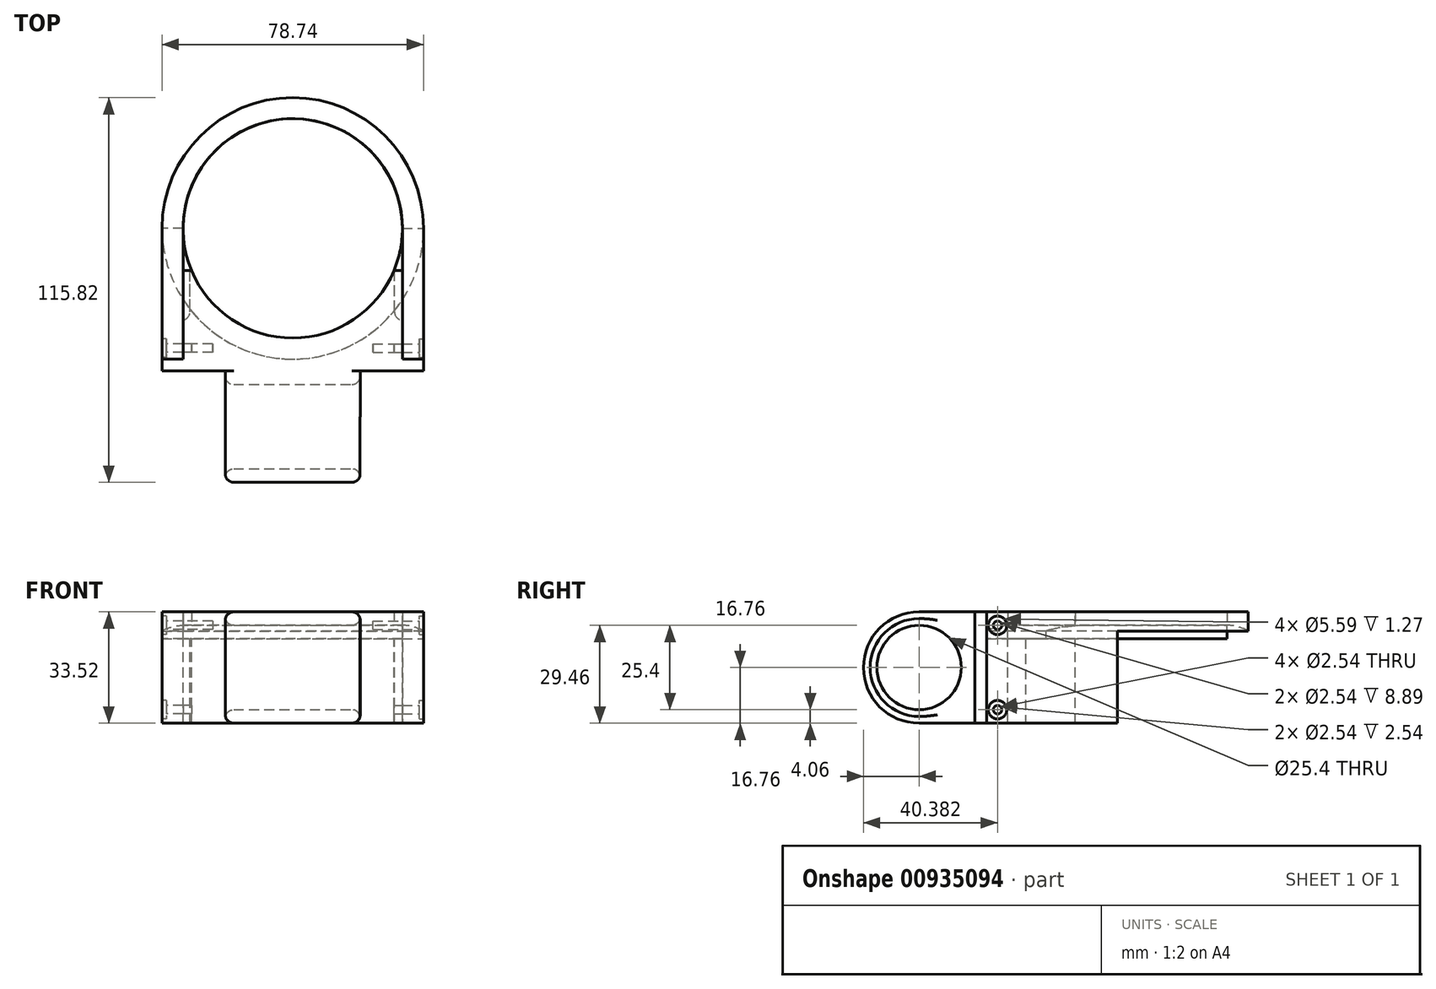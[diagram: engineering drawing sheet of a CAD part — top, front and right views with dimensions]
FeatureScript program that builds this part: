
annotation { "Feature Type Name" : "Feature", "Feature Type Description" : "" }
export const myFeature = defineFeature(function(context is Context, id is Id, definition is map)
    precondition{}
    {
        {
            var Q0;
            Q0=qCreatedBy(makeId("Top.planeOp"),FACE);
            var sketch = newSketch(context, id + "F0", { "sketchPlane" : qUnion([Q0])});
            skCircle(sketch, "E0", {"center": v(0, 0) * mm, "radius": 33.02 * mm});
            skCircle(sketch, "E1", {"center": v(0, 0) * mm, "radius": 39.37 * mm});
            skLineSegment(sketch, "E2", {"start": v(0, -39.37) * mm, "end": v(0, -59.7) * mm});
            skLineSegment(sketch, "E3", {"start": v(0, -59.7) * mm, "end": v(-19.05, -59.7) * mm});
            skLineSegment(sketch, "E4.bottom", {"start": v(-19.05, -59.7) * mm, "end": v(19.05, -59.7) * mm});
            skLineSegment(sketch, "E4.top", {"start": v(-19.05, -39.37) * mm, "end": v(19.05, -39.37) * mm});
            skLineSegment(sketch, "E4.left", {"start": v(-19.05, -59.7) * mm, "end": v(-19.05, -39.37) * mm});
            skLineSegment(sketch, "E4.right", {"start": v(19.05, -59.7) * mm, "end": v(19.05, -39.37) * mm});
            skPoint(sketch, "E4.middle", {"position": v(0, -49.53) * mm});
            skLineSegment(sketch, "E5.bottom", {"start": v(0, -59.7) * mm, "end": v(-39.37, -59.7) * mm});
            skLineSegment(sketch, "E5.top", {"start": v(0, 0) * mm, "end": v(-39.37, 0) * mm});
            skLineSegment(sketch, "E5.left", {"start": v(0, -59.7) * mm, "end": v(0, 0) * mm});
            skLineSegment(sketch, "E5.right", {"start": v(-39.37, -59.7) * mm, "end": v(-39.37, 0) * mm});
            skLineSegment(sketch, "E6.bottom", {"start": v(0, -59.7) * mm, "end": v(39.37, -59.7) * mm});
            skLineSegment(sketch, "E6.top", {"start": v(0, 0) * mm, "end": v(39.37, 0) * mm});
            skLineSegment(sketch, "E6.right", {"start": v(39.37, -59.7) * mm, "end": v(39.37, 0) * mm});
            skLineSegment(sketch, "E7", {"start": v(-33.02, 0) * mm, "end": v(-33.02, -59.7) * mm});
            skLineSegment(sketch, "E8", {"start": v(33.02, 0) * mm, "end": v(33.02, -59.7) * mm});
            skLineSegment(sketch, "E9", {"start": v(33.02, 0) * mm, "end": v(33.02, -12.7) * mm});
            skLineSegment(sketch, "E10", {"start": v(33.02, -12.7) * mm, "end": v(-33.02, -12.7) * mm});
            skLineSegment(sketch, "E11", {"start": v(-19.05, -39.37) * mm, "end": v(-39.37, -39.37) * mm});
            skLineSegment(sketch, "E12", {"start": v(-39.37, -39.37) * mm, "end": v(19.05, -39.37) * mm});
            skLineSegment(sketch, "E13", {"start": v(19.05, -39.37) * mm, "end": v(39.37, -39.37) * mm});
            skLineSegment(sketch, "E14", {"start": v(30.48, -12.7) * mm, "end": v(30.48, -24.92) * mm});
            skLineSegment(sketch, "E15", {"start": v(-30.48, -12.7) * mm, "end": v(-30.48, -24.92) * mm});
            skSolve(sketch);
        }
        {
            var Q0;
            {var subQ0=sQuery(id+"F0.wireOp",EDGE,"E5.top");var subQ1=sQuery(id+"F0.wireOp",EDGE,"E0");var subQ2=makeQuery(id+"F0.imprint","INTERSECT",VERTEX,{"derivedFrom":[subQ1,subQ0,sQuery(id+"F0.wireOp",EDGE,"E7")]});Q0=makeQuery(id+"F0.imprint","IMPRINT",FACE,{"disambiguationData":[TD([[makeQuery(id+"F0.imprint","IMPRINT",EDGE,{"disambiguationData":[TD([[subQ2,1.0]])],"derivedFrom":subQ1}),-1.0]])]});}
            var Q1;
            {var subQ1=sQuery(id+"F0.wireOp",EDGE,"E1");var subQ3=sQuery(id+"F0.wireOp",EDGE,"E8");var subQ4=makeQuery(id+"F0.imprint","INTERSECT",VERTEX,{"derivedFrom":[subQ1,subQ3]});Q1=makeQuery(id+"F0.imprint","IMPRINT",FACE,{"disambiguationData":[TD([[makeQuery(id+"F0.imprint","IMPRINT",EDGE,{"disambiguationData":[TD([[subQ4,1.0]])],"derivedFrom":subQ3}),1.0]])]});}
            var Q2;
            {var subQ3=sQuery(id+"F0.wireOp",EDGE,"E8");var subQ5=sQuery(id+"F0.wireOp",EDGE,"E13");var subQ7=makeQuery(id+"F0.imprint","INTERSECT",VERTEX,{"derivedFrom":[subQ3,subQ5]});Q2=makeQuery(id+"F0.imprint","IMPRINT",FACE,{"disambiguationData":[TD([[makeQuery(id+"F0.imprint","IMPRINT",EDGE,{"disambiguationData":[TD([[subQ7,1.0]])],"derivedFrom":subQ3}),1.0]])]});}
            var Q3;
            {var subQ1=sQuery(id+"F0.wireOp",EDGE,"E1");var subQ3=sQuery(id+"F0.wireOp",EDGE,"E7");var subQ4=makeQuery(id+"F0.imprint","INTERSECT",VERTEX,{"derivedFrom":[subQ1,subQ3]});Q3=makeQuery(id+"F0.imprint","IMPRINT",FACE,{"disambiguationData":[TD([[makeQuery(id+"F0.imprint","IMPRINT",EDGE,{"disambiguationData":[TD([[subQ4,1.0]])],"derivedFrom":subQ3}),-1.0]])]});}
            var Q4;
            {var subQ3=sQuery(id+"F0.wireOp",EDGE,"E7");var subQ5=sQuery(id+"F0.wireOp",EDGE,"E11");var subQ7=makeQuery(id+"F0.imprint","INTERSECT",VERTEX,{"derivedFrom":[subQ3,subQ5]});Q4=makeQuery(id+"F0.imprint","IMPRINT",FACE,{"disambiguationData":[TD([[makeQuery(id+"F0.imprint","IMPRINT",EDGE,{"disambiguationData":[TD([[subQ7,1.0]])],"derivedFrom":subQ3}),-1.0]])]});}
            extrude(context, id + "F1", {"entities" : qUnion([Q0, Q1, Q2, Q3, Q4]), "depth" : 4.06 * mm, "offsetDistance" : 25.4 * mm});
        }
        {
            var Q0;
            {var subQ3=sQuery(id+"F0.wireOp",EDGE,"E14");Q0=makeQuery(id+"F0.imprint","IMPRINT",FACE,{"disambiguationData":[TD([[makeQuery(id+"F0.imprint","IMPRINT",EDGE,{"derivedFrom":subQ3}),-1.0]])]});}
            var Q1;
            {var subQ1=sQuery(id+"F0.wireOp",EDGE,"E7");var subQ3=sQuery(id+"F0.wireOp",EDGE,"E1");var subQ4=makeQuery(id+"F0.imprint","INTERSECT",VERTEX,{"derivedFrom":[subQ3,subQ1]});Q1=makeQuery(id+"F0.imprint","IMPRINT",FACE,{"disambiguationData":[TD([[makeQuery(id+"F0.imprint","IMPRINT",EDGE,{"disambiguationData":[TD([[subQ4,-1.0]])],"derivedFrom":subQ3}),-1.0]])]});}
            var Q2;
            {var subQ1=sQuery(id+"F0.wireOp",EDGE,"E1");var subQ5=sQuery(id+"F0.wireOp",EDGE,"E8");var subQ7=makeQuery(id+"F0.imprint","INTERSECT",VERTEX,{"derivedFrom":[subQ1,subQ5]});Q2=makeQuery(id+"F0.imprint","IMPRINT",FACE,{"disambiguationData":[TD([[makeQuery(id+"F0.imprint","IMPRINT",EDGE,{"disambiguationData":[TD([[subQ7,1.0]])],"derivedFrom":subQ1}),-1.0]])]});}
            var Q3;
            {var subQ3=sQuery(id+"F0.wireOp",EDGE,"E15");Q3=makeQuery(id+"F0.imprint","IMPRINT",FACE,{"disambiguationData":[TD([[makeQuery(id+"F0.imprint","IMPRINT",EDGE,{"derivedFrom":subQ3}),1.0]])]});}
            var Q4;
            {var subQ3=sQuery(id+"F0.wireOp",EDGE,"E15");Q4=makeQuery(id+"F0.imprint","IMPRINT",FACE,{"disambiguationData":[TD([[makeQuery(id+"F0.imprint","IMPRINT",EDGE,{"derivedFrom":subQ3}),-1.0]])]});}
            var Q5;
            {var subQ3=sQuery(id+"F0.wireOp",EDGE,"E14");Q5=makeQuery(id+"F0.imprint","IMPRINT",FACE,{"disambiguationData":[TD([[makeQuery(id+"F0.imprint","IMPRINT",EDGE,{"derivedFrom":subQ3}),1.0]])]});}
            var Q6;
            {var subQ0=sQuery(id+"F0.wireOp",EDGE,"E5.right");var subQ1=sQuery(id+"F0.wireOp",EDGE,"E5.bottom");var subQ2=makeQuery(id+"F0.imprint","INTERSECT",VERTEX,{"derivedFrom":[subQ1,subQ0]});Q6=makeQuery(id+"F0.imprint","IMPRINT",FACE,{"disambiguationData":[TD([[makeQuery(id+"F0.imprint","IMPRINT",EDGE,{"disambiguationData":[TD([[subQ2,1.0]])],"derivedFrom":subQ1}),-1.0]])]});}
            var Q7;
            {var subQ0=sQuery(id+"F0.wireOp",EDGE,"E4.left");Q7=makeQuery(id+"F0.imprint","IMPRINT",FACE,{"disambiguationData":[TD([[makeQuery(id+"F0.imprint","IMPRINT",EDGE,{"derivedFrom":subQ0}),1.0]])]});}
            var Q8;
            {var subQ0=sQuery(id+"F0.wireOp",EDGE,"E2");Q8=makeQuery(id+"F0.imprint","IMPRINT",FACE,{"disambiguationData":[TD([[makeQuery(id+"F0.imprint","IMPRINT",EDGE,{"derivedFrom":subQ0}),-1.0]])]});}
            var Q9;
            {var subQ0=sQuery(id+"F0.wireOp",EDGE,"E2");Q9=makeQuery(id+"F0.imprint","IMPRINT",FACE,{"disambiguationData":[TD([[makeQuery(id+"F0.imprint","IMPRINT",EDGE,{"derivedFrom":subQ0}),1.0]])]});}
            var Q10;
            {var subQ0=sQuery(id+"F0.wireOp",EDGE,"E4.right");Q10=makeQuery(id+"F0.imprint","IMPRINT",FACE,{"disambiguationData":[TD([[makeQuery(id+"F0.imprint","IMPRINT",EDGE,{"derivedFrom":subQ0}),-1.0]])]});}
            var Q11;
            {var subQ0=sQuery(id+"F0.wireOp",EDGE,"E6.right");var subQ1=sQuery(id+"F0.wireOp",EDGE,"E6.bottom");var subQ2=makeQuery(id+"F0.imprint","INTERSECT",VERTEX,{"derivedFrom":[subQ1,subQ0]});Q11=makeQuery(id+"F0.imprint","IMPRINT",FACE,{"disambiguationData":[TD([[makeQuery(id+"F0.imprint","IMPRINT",EDGE,{"disambiguationData":[TD([[subQ2,1.0]])],"derivedFrom":subQ1}),1.0]])]});}
            extrude(context, id + "F2", {"entities" : qUnion([Q0, Q1, Q2, Q3, Q4, Q5, Q6, Q7, Q8, Q9, Q10, Q11]), "depth" : 4.06 * mm, "offsetDistance" : 25.4 * mm});
        }
        {
            var Q0;
            {var subQ0=sQuery(id+"F0.wireOp",EDGE,"E5.top");var subQ1=sQuery(id+"F0.wireOp",EDGE,"E0");var subQ2=makeQuery(id+"F0.imprint","INTERSECT",VERTEX,{"derivedFrom":[subQ1,subQ0,sQuery(id+"F0.wireOp",EDGE,"E7")]});Q0=makeQuery(id+"F0.imprint","IMPRINT",FACE,{"disambiguationData":[TD([[makeQuery(id+"F0.imprint","IMPRINT",EDGE,{"disambiguationData":[TD([[subQ2,1.0]])],"derivedFrom":subQ1}),1.0]])]});}
            var Q1;
            {var subQ0=sQuery(id+"F0.wireOp",EDGE,"E10");var subQ5=sQuery(id+"F0.wireOp",EDGE,"E5.left");var subQ7=makeQuery(id+"F0.imprint","INTERSECT",VERTEX,{"derivedFrom":[subQ5,subQ0]});Q1=makeQuery(id+"F0.imprint","IMPRINT",FACE,{"disambiguationData":[TD([[makeQuery(id+"F0.imprint","IMPRINT",EDGE,{"disambiguationData":[TD([[subQ7,-1.0]])],"derivedFrom":subQ5}),-1.0]])]});}
            var Q2;
            {var subQ0=sQuery(id+"F0.wireOp",EDGE,"E10");var subQ5=sQuery(id+"F0.wireOp",EDGE,"E5.left");var subQ7=makeQuery(id+"F0.imprint","INTERSECT",VERTEX,{"derivedFrom":[subQ5,subQ0]});Q2=makeQuery(id+"F0.imprint","IMPRINT",FACE,{"disambiguationData":[TD([[makeQuery(id+"F0.imprint","IMPRINT",EDGE,{"disambiguationData":[TD([[subQ7,-1.0]])],"derivedFrom":subQ5}),1.0]])]});}
            var Q3;
            {var subQ0=sQuery(id+"F0.wireOp",EDGE,"E5.left");var subQ1=sQuery(id+"F0.wireOp",EDGE,"E0");var subQ2=makeQuery(id+"F0.imprint","INTERSECT",VERTEX,{"derivedFrom":[subQ1,subQ0]});Q3=makeQuery(id+"F0.imprint","IMPRINT",FACE,{"disambiguationData":[TD([[makeQuery(id+"F0.imprint","IMPRINT",EDGE,{"disambiguationData":[TD([[subQ2,-1.0]])],"derivedFrom":subQ0}),1.0]])]});}
            var Q4;
            {var subQ0=sQuery(id+"F0.wireOp",EDGE,"E5.left");var subQ1=sQuery(id+"F0.wireOp",EDGE,"E0");var subQ2=makeQuery(id+"F0.imprint","INTERSECT",VERTEX,{"derivedFrom":[subQ1,subQ0]});Q4=makeQuery(id+"F0.imprint","IMPRINT",FACE,{"disambiguationData":[TD([[makeQuery(id+"F0.imprint","IMPRINT",EDGE,{"disambiguationData":[TD([[subQ2,-1.0]])],"derivedFrom":subQ0}),-1.0]])]});}
            extrude(context, id + "F3", {"entities" : qUnion([Q0, Q1, Q2, Q3, Q4]), "oppositeDirection" : true, "depth" : 4.06 * mm, "offsetDistance" : 25.4 * mm});
        }
        {
            var Q0;
            {var subQ0=sQuery(id+"F0.wireOp",EDGE,"E5.top");var subQ1=sQuery(id+"F0.wireOp",EDGE,"E0");var subQ2=makeQuery(id+"F0.imprint","INTERSECT",VERTEX,{"derivedFrom":[subQ1,subQ0,sQuery(id+"F0.wireOp",EDGE,"E7")]});Q0=makeQuery(id+"F0.imprint","IMPRINT",FACE,{"disambiguationData":[TD([[makeQuery(id+"F0.imprint","IMPRINT",EDGE,{"disambiguationData":[TD([[subQ2,1.0]])],"derivedFrom":subQ1}),-1.0]])]});}
            extrude(context, id + "F4", {"entities" : qUnion([Q0]), "oppositeDirection" : true, "depth" : 4.06 * mm, "offsetDistance" : 25.4 * mm});
        }
        {
            var Q0;
            {var subQ0=sQuery(id+"F0.wireOp",EDGE,"E5.right");var subQ1=sQuery(id+"F0.wireOp",EDGE,"E5.bottom");var subQ2=makeQuery(id+"F0.imprint","INTERSECT",VERTEX,{"derivedFrom":[subQ1,subQ0]});Q0=makeQuery(id+"F0.imprint","IMPRINT",FACE,{"disambiguationData":[TD([[makeQuery(id+"F0.imprint","IMPRINT",EDGE,{"disambiguationData":[TD([[subQ2,1.0]])],"derivedFrom":subQ1}),-1.0]])]});}
            var Q1;
            {var subQ0=sQuery(id+"F0.wireOp",EDGE,"E4.left");Q1=makeQuery(id+"F0.imprint","IMPRINT",FACE,{"disambiguationData":[TD([[makeQuery(id+"F0.imprint","IMPRINT",EDGE,{"derivedFrom":subQ0}),1.0]])]});}
            var Q2;
            {var subQ1=sQuery(id+"F0.wireOp",EDGE,"E7");var subQ3=sQuery(id+"F0.wireOp",EDGE,"E1");var subQ4=makeQuery(id+"F0.imprint","INTERSECT",VERTEX,{"derivedFrom":[subQ3,subQ1]});Q2=makeQuery(id+"F0.imprint","IMPRINT",FACE,{"disambiguationData":[TD([[makeQuery(id+"F0.imprint","IMPRINT",EDGE,{"disambiguationData":[TD([[subQ4,-1.0]])],"derivedFrom":subQ3}),-1.0]])]});}
            var Q3;
            {var subQ0=sQuery(id+"F0.wireOp",EDGE,"E2");Q3=makeQuery(id+"F0.imprint","IMPRINT",FACE,{"disambiguationData":[TD([[makeQuery(id+"F0.imprint","IMPRINT",EDGE,{"derivedFrom":subQ0}),-1.0]])]});}
            var Q4;
            {var subQ0=sQuery(id+"F0.wireOp",EDGE,"E2");Q4=makeQuery(id+"F0.imprint","IMPRINT",FACE,{"disambiguationData":[TD([[makeQuery(id+"F0.imprint","IMPRINT",EDGE,{"derivedFrom":subQ0}),1.0]])]});}
            var Q5;
            {var subQ0=sQuery(id+"F0.wireOp",EDGE,"E4.right");Q5=makeQuery(id+"F0.imprint","IMPRINT",FACE,{"disambiguationData":[TD([[makeQuery(id+"F0.imprint","IMPRINT",EDGE,{"derivedFrom":subQ0}),-1.0]])]});}
            var Q6;
            {var subQ0=sQuery(id+"F0.wireOp",EDGE,"E6.right");var subQ1=sQuery(id+"F0.wireOp",EDGE,"E6.bottom");var subQ2=makeQuery(id+"F0.imprint","INTERSECT",VERTEX,{"derivedFrom":[subQ1,subQ0]});Q6=makeQuery(id+"F0.imprint","IMPRINT",FACE,{"disambiguationData":[TD([[makeQuery(id+"F0.imprint","IMPRINT",EDGE,{"disambiguationData":[TD([[subQ2,1.0]])],"derivedFrom":subQ1}),1.0]])]});}
            var Q7;
            {var subQ1=sQuery(id+"F0.wireOp",EDGE,"E1");var subQ5=sQuery(id+"F0.wireOp",EDGE,"E8");var subQ7=makeQuery(id+"F0.imprint","INTERSECT",VERTEX,{"derivedFrom":[subQ1,subQ5]});Q7=makeQuery(id+"F0.imprint","IMPRINT",FACE,{"disambiguationData":[TD([[makeQuery(id+"F0.imprint","IMPRINT",EDGE,{"disambiguationData":[TD([[subQ7,1.0]])],"derivedFrom":subQ1}),-1.0]])]});}
            var Q8;
            {var subQ3=sQuery(id+"F0.wireOp",EDGE,"E14");Q8=makeQuery(id+"F0.imprint","IMPRINT",FACE,{"disambiguationData":[TD([[makeQuery(id+"F0.imprint","IMPRINT",EDGE,{"derivedFrom":subQ3}),-1.0]])]});}
            var Q9;
            {var subQ3=sQuery(id+"F0.wireOp",EDGE,"E15");Q9=makeQuery(id+"F0.imprint","IMPRINT",FACE,{"disambiguationData":[TD([[makeQuery(id+"F0.imprint","IMPRINT",EDGE,{"derivedFrom":subQ3}),-1.0]])]});}
            var Q10;
            {var subQ3=sQuery(id+"F0.wireOp",EDGE,"E15");Q10=makeQuery(id+"F0.imprint","IMPRINT",FACE,{"disambiguationData":[TD([[makeQuery(id+"F0.imprint","IMPRINT",EDGE,{"derivedFrom":subQ3}),1.0]])]});}
            var Q11;
            {var subQ3=sQuery(id+"F0.wireOp",EDGE,"E14");Q11=makeQuery(id+"F0.imprint","IMPRINT",FACE,{"disambiguationData":[TD([[makeQuery(id+"F0.imprint","IMPRINT",EDGE,{"derivedFrom":subQ3}),1.0]])]});}
            extrude(context, id + "F5", {"entities" : qUnion([Q0, Q1, Q2, Q3, Q4, Q5, Q6, Q7, Q8, Q9, Q10, Q11]), "oppositeDirection" : true, "depth" : 4.06 * mm, "offsetDistance" : 25.4 * mm});
        }
        {
            var Q0;
            {var subQ3=sQuery(id+"F0.wireOp",EDGE,"E7");var subQ5=sQuery(id+"F0.wireOp",EDGE,"E11");var subQ7=makeQuery(id+"F0.imprint","INTERSECT",VERTEX,{"derivedFrom":[subQ3,subQ5]});Q0=makeQuery(id+"F0.imprint","IMPRINT",FACE,{"disambiguationData":[TD([[makeQuery(id+"F0.imprint","IMPRINT",EDGE,{"disambiguationData":[TD([[subQ7,1.0]])],"derivedFrom":subQ3}),-1.0]])]});}
            var Q1;
            {var subQ1=sQuery(id+"F0.wireOp",EDGE,"E1");var subQ3=sQuery(id+"F0.wireOp",EDGE,"E7");var subQ4=makeQuery(id+"F0.imprint","INTERSECT",VERTEX,{"derivedFrom":[subQ1,subQ3]});Q1=makeQuery(id+"F0.imprint","IMPRINT",FACE,{"disambiguationData":[TD([[makeQuery(id+"F0.imprint","IMPRINT",EDGE,{"disambiguationData":[TD([[subQ4,1.0]])],"derivedFrom":subQ3}),-1.0]])]});}
            var Q2;
            {var subQ1=sQuery(id+"F0.wireOp",EDGE,"E1");var subQ3=sQuery(id+"F0.wireOp",EDGE,"E8");var subQ4=makeQuery(id+"F0.imprint","INTERSECT",VERTEX,{"derivedFrom":[subQ1,subQ3]});Q2=makeQuery(id+"F0.imprint","IMPRINT",FACE,{"disambiguationData":[TD([[makeQuery(id+"F0.imprint","IMPRINT",EDGE,{"disambiguationData":[TD([[subQ4,1.0]])],"derivedFrom":subQ3}),1.0]])]});}
            var Q3;
            {var subQ3=sQuery(id+"F0.wireOp",EDGE,"E8");var subQ5=sQuery(id+"F0.wireOp",EDGE,"E13");var subQ7=makeQuery(id+"F0.imprint","INTERSECT",VERTEX,{"derivedFrom":[subQ3,subQ5]});Q3=makeQuery(id+"F0.imprint","IMPRINT",FACE,{"disambiguationData":[TD([[makeQuery(id+"F0.imprint","IMPRINT",EDGE,{"disambiguationData":[TD([[subQ7,1.0]])],"derivedFrom":subQ3}),1.0]])]});}
            extrude(context, id + "F6", {"entities" : qUnion([Q0, Q1, Q2, Q3]), "oppositeDirection" : true, "depth" : 4.06 * mm, "offsetDistance" : 25.4 * mm});
        }
        {
            var Q0;
            Q0=makeQuery(id+"F6.opExtrude","SWEPT_FACE",FACE,{"disambiguationData":[OSD([sQuery(id+"F0.wireOp",EDGE,"E5.top")])]});
            var sketch = newSketch(context, id + "F7", { "sketchPlane" : qUnion([Q0])});
            skLineSegment(sketch, "E16", {"start": v(33.02, 0) * mm, "end": v(33.02, -12.7) * mm});
            skArc(sketch, "E17", {"start": v(33.02, 0) * mm, "mid": v(42, -3.72) * mm, "end": v(45.72, -12.7) * mm});
            skLineSegment(sketch, "E18", {"start": v(33.02, -12.7) * mm, "end": v(45.72, -12.7) * mm});
            skLineSegment(sketch, "E19", {"start": v(33.02, -12.7) * mm, "end": v(33.02, -38.1) * mm});
            skLineSegment(sketch, "E20.bottom", {"start": v(45.72, -12.7) * mm, "end": v(33.02, -12.7) * mm});
            skLineSegment(sketch, "E20.top", {"start": v(45.72, -38.1) * mm, "end": v(33.02, -38.1) * mm});
            skLineSegment(sketch, "E20.left", {"start": v(45.72, -12.7) * mm, "end": v(45.72, -38.1) * mm});
            skSolve(sketch);
        }
        {
            var Q0;
            Q0=makeQuery(id+"F5.opExtrude","CAP_FACE",FACE,{"disambiguationData":[OSD([sQuery(id+"F0.wireOp",EDGE,"E0"),sQuery(id+"F0.wireOp",EDGE,"E3"),sQuery(id+"F0.wireOp",EDGE,"E4.bottom"),sQuery(id+"F0.wireOp",EDGE,"E5.bottom"),sQuery(id+"F0.wireOp",EDGE,"E5.right"),sQuery(id+"F0.wireOp",EDGE,"E6.bottom"),sQuery(id+"F0.wireOp",EDGE,"E6.right"),sQuery(id+"F0.wireOp",EDGE,"E7"),sQuery(id+"F0.wireOp",EDGE,"E8"),sQuery(id+"F0.wireOp",EDGE,"E10"),sQuery(id+"F0.wireOp",EDGE,"E11"),sQuery(id+"F0.wireOp",EDGE,"E13")])],"isStart":false});
            var Q1;
            Q1=makeQuery(id+"F6.opExtrude","CAP_FACE",FACE,{"disambiguationData":[OSD([sQuery(id+"F0.wireOp",EDGE,"E5.top"),sQuery(id+"F0.wireOp",EDGE,"E5.right"),sQuery(id+"F0.wireOp",EDGE,"E7"),sQuery(id+"F0.wireOp",EDGE,"E11")])],"isStart":false});
            var Q2;
            Q2=makeQuery(id+"F6.opExtrude","CAP_FACE",FACE,{"disambiguationData":[OSD([sQuery(id+"F0.wireOp",EDGE,"E6.top"),sQuery(id+"F0.wireOp",EDGE,"E6.right"),sQuery(id+"F0.wireOp",EDGE,"E8"),sQuery(id+"F0.wireOp",EDGE,"E13")])],"isStart":false});
            extrude(context, id + "F8", {"entities" : qUnion([Q0, Q1, Q2]), "depth" : 25.4 * mm, "offsetDistance" : 25.4 * mm});
        }
        {
            var Q0;
            {var subQ2=sQuery(id+"F7.wireOp",EDGE,"E20.bottom");Q0=makeQuery(id+"F7.imprint","IMPRINT",FACE,{"disambiguationData":[TD([[makeQuery(id+"F7.imprint","IMPRINT",EDGE,{"derivedFrom":subQ2}),-1.0]])]});}
            var Q1;
            Q1=makeQuery(id+"F7.imprint","IMPRINT",FACE,{"disambiguationData":[TD([[makeQuery(id+"F7.imprint","IMPRINT",EDGE,{"derivedFrom":sQuery(id+"F7.wireOp",EDGE,"E20.bottom")}),1.0]])]});
            var Q2;
            {var subQ2=sQuery(id+"F0.wireOp",EDGE,"E5.top");var subQ4=makeQuery(id+"F6.opExtrude","CAP_EDGE",EDGE,{"disambiguationData":[OSD([subQ2])],"isStart":false});Q2=makeQuery(id+"F7.imprint","IMPRINT",FACE,{"disambiguationData":[TD([[makeQuery(id+"F7.imprint","IMPRINT",EDGE,{"derivedFrom":subQ4}),1.0]])]});}
            var Q3;
            Q3=makeQuery(id+"F1.opExtrude","CAP_EDGE",EDGE,{"disambiguationData":[OSD([sQuery(id+"F0.wireOp",EDGE,"E0")])],"isStart":true});
            revolve(context, id + "F9", {"operationType" : NewBodyOperationType.REMOVE, "surfaceOperationType" : NewSurfaceOperationType.NEW, "entities" : qUnion([Q0, Q1, Q2]), "axis" : qUnion([Q3]), "revolveType" : RevolveType.FULL, "oppositeDirection" : true});
        }
        {
            var Q0;
            Q0=makeQuery(id+"F8.opExtrude","CAP_FACE",FACE,{"disambiguationData":[OSD([sQuery(id+"F0.wireOp",EDGE,"E5.top"),sQuery(id+"F0.wireOp",EDGE,"E5.right"),sQuery(id+"F0.wireOp",EDGE,"E7"),sQuery(id+"F0.wireOp",EDGE,"E11")])],"isStart":false});
            var sketch = newSketch(context, id + "F10", { "sketchPlane" : qUnion([Q0])});
            skLineSegment(sketch, "E21", {"start": v(-36.44, 27.62) * mm, "end": v(-39.37, 27.62) * mm});
            skLineSegment(sketch, "E22.bottom", {"start": v(-39.37, 27.62) * mm, "end": v(-30.94, 27.62) * mm});
            skLineSegment(sketch, "E22.top", {"start": v(-39.37, 8.01) * mm, "end": v(-30.94, 8.01) * mm});
            skLineSegment(sketch, "E22.left", {"start": v(-39.37, 27.62) * mm, "end": v(-39.37, 8.01) * mm});
            skLineSegment(sketch, "E22.right", {"start": v(-30.94, 27.62) * mm, "end": v(-30.94, 8.01) * mm});
            skSolve(sketch);
        }
        {
            var Q0;
            Q0=makeQuery(id+"F8.opExtrude","CAP_FACE",FACE,{"disambiguationData":[OSD([sQuery(id+"F0.wireOp",EDGE,"E6.top"),sQuery(id+"F0.wireOp",EDGE,"E6.right"),sQuery(id+"F0.wireOp",EDGE,"E8"),sQuery(id+"F0.wireOp",EDGE,"E13")])],"isStart":false});
            var sketch = newSketch(context, id + "F11", { "sketchPlane" : qUnion([Q0])});
            skLineSegment(sketch, "E23", {"start": v(36.44, 27.62) * mm, "end": v(39.37, 27.62) * mm});
            skLineSegment(sketch, "E24.bottom", {"start": v(39.37, 27.62) * mm, "end": v(30.62, 27.62) * mm});
            skLineSegment(sketch, "E24.top", {"start": v(39.37, 1.89) * mm, "end": v(30.62, 1.89) * mm});
            skLineSegment(sketch, "E24.left", {"start": v(39.37, 27.62) * mm, "end": v(39.37, 1.89) * mm});
            skLineSegment(sketch, "E24.right", {"start": v(30.62, 27.62) * mm, "end": v(30.62, 1.89) * mm});
            skSolve(sketch);
        }
        {
            var Q0;
            {var subQ0=sQuery(id+"F11.wireOp",EDGE,"E24.left");var subQ1=sQuery(id+"F11.wireOp",EDGE,"E24.bottom");var subQ2=sQuery(id+"F0.wireOp",EDGE,"E6.right");var subQ3=makeQuery(id+"F11.imprint","INTERSECT",VERTEX,{"derivedFrom":[makeQuery(id+"F8.opExtrude","CAP_EDGE",EDGE,{"disambiguationData":[OSD([subQ2]),TDD([makeQuery(id+"F6.opExtrude","CAP_EDGE",EDGE,{"disambiguationData":[OSD([subQ2])],"isStart":false})])],"isStart":false}),subQ1,subQ0]});Q0=makeQuery(id+"F11.imprint","IMPRINT",FACE,{"disambiguationData":[TD([[makeQuery(id+"F11.imprint","IMPRINT",EDGE,{"disambiguationData":[TD([[subQ3,-1.0]])],"derivedFrom":subQ1}),1.0]])]});}
            var Q1;
            {var subQ4=sQuery(id+"F11.wireOp",EDGE,"E24.top");Q1=makeQuery(id+"F11.imprint","IMPRINT",FACE,{"disambiguationData":[TD([[makeQuery(id+"F11.imprint","IMPRINT",EDGE,{"derivedFrom":subQ4}),-1.0]])]});}
            var Q2;
            {var subQ4=sQuery(id+"F10.wireOp",EDGE,"E22.top");Q2=makeQuery(id+"F10.imprint","IMPRINT",FACE,{"disambiguationData":[TD([[makeQuery(id+"F10.imprint","IMPRINT",EDGE,{"derivedFrom":subQ4}),1.0]])]});}
            var Q3;
            {var subQ0=sQuery(id+"F10.wireOp",EDGE,"E22.left");var subQ1=sQuery(id+"F10.wireOp",EDGE,"E22.bottom");var subQ2=sQuery(id+"F0.wireOp",EDGE,"E5.right");var subQ3=makeQuery(id+"F10.imprint","INTERSECT",VERTEX,{"derivedFrom":[makeQuery(id+"F8.opExtrude","CAP_EDGE",EDGE,{"disambiguationData":[OSD([subQ2]),TDD([makeQuery(id+"F6.opExtrude","CAP_EDGE",EDGE,{"disambiguationData":[OSD([subQ2])],"isStart":false})])],"isStart":false}),subQ1,subQ0]});Q3=makeQuery(id+"F10.imprint","IMPRINT",FACE,{"disambiguationData":[TD([[makeQuery(id+"F10.imprint","IMPRINT",EDGE,{"disambiguationData":[TD([[subQ3,-1.0]])],"derivedFrom":subQ1}),-1.0]])]});}
            extrude(context, id + "F12", {"entities" : qUnion([Q0, Q1, Q2, Q3]), "operationType" : NewBodyOperationType.REMOVE, "oppositeDirection" : true, "depth" : 25.4 * mm, "offsetDistance" : 25.4 * mm});
        }
        {
            var Q0;
            Q0=makeQuery(id+"F8.opExtrude","SWEPT_BODY",BODY,{"disambiguationData":[OSD([sQuery(id+"F0.wireOp",EDGE,"E5.top"),sQuery(id+"F0.wireOp",EDGE,"E5.right"),sQuery(id+"F0.wireOp",EDGE,"E7"),sQuery(id+"F0.wireOp",EDGE,"E11")])]});
            var Q1;
            Q1=makeQuery(id+"F6.opExtrude","SWEPT_BODY",BODY,{"disambiguationData":[OSD([sQuery(id+"F0.wireOp",EDGE,"E5.top"),sQuery(id+"F0.wireOp",EDGE,"E5.right"),sQuery(id+"F0.wireOp",EDGE,"E7"),sQuery(id+"F0.wireOp",EDGE,"E11")])]});
            var Q2;
            Q2=makeQuery(id+"F1.opExtrude","SWEPT_BODY",BODY,{"disambiguationData":[OSD([sQuery(id+"F0.wireOp",EDGE,"E0"),sQuery(id+"F0.wireOp",EDGE,"E1"),sQuery(id+"F0.wireOp",EDGE,"E5.right"),sQuery(id+"F0.wireOp",EDGE,"E6.right"),sQuery(id+"F0.wireOp",EDGE,"E7"),sQuery(id+"F0.wireOp",EDGE,"E8"),sQuery(id+"F0.wireOp",EDGE,"E11"),sQuery(id+"F0.wireOp",EDGE,"E13")])]});
            var Q3;
            Q3=makeQuery(id+"F4.opExtrude","SWEPT_BODY",BODY,{"disambiguationData":[OSD([sQuery(id+"F0.wireOp",EDGE,"E0"),sQuery(id+"F0.wireOp",EDGE,"E1"),sQuery(id+"F0.wireOp",EDGE,"E5.top"),sQuery(id+"F0.wireOp",EDGE,"E6.top")])]});
            var Q4;
            Q4=makeQuery(id+"F6.opExtrude","SWEPT_BODY",BODY,{"disambiguationData":[OSD([sQuery(id+"F0.wireOp",EDGE,"E6.top"),sQuery(id+"F0.wireOp",EDGE,"E6.right"),sQuery(id+"F0.wireOp",EDGE,"E8"),sQuery(id+"F0.wireOp",EDGE,"E13")])]});
            var Q5;
            Q5=makeQuery(id+"F8.opExtrude","SWEPT_BODY",BODY,{"disambiguationData":[OSD([sQuery(id+"F0.wireOp",EDGE,"E6.top"),sQuery(id+"F0.wireOp",EDGE,"E6.right"),sQuery(id+"F0.wireOp",EDGE,"E8"),sQuery(id+"F0.wireOp",EDGE,"E13")])]});
            booleanBodies(context, id + "F13", {"operationType" : BooleanOperationType.UNION, "tools" : qUnion([Q0, Q1, Q2, Q3, Q4, Q5])});
        }
        {
            var Q0;
            Q0=makeQuery(id+"F8.opExtrude","SWEPT_BODY",BODY,{"disambiguationData":[OSD([sQuery(id+"F0.wireOp",EDGE,"E0"),sQuery(id+"F0.wireOp",EDGE,"E3"),sQuery(id+"F0.wireOp",EDGE,"E4.bottom"),sQuery(id+"F0.wireOp",EDGE,"E5.bottom"),sQuery(id+"F0.wireOp",EDGE,"E5.right"),sQuery(id+"F0.wireOp",EDGE,"E6.bottom"),sQuery(id+"F0.wireOp",EDGE,"E6.right"),sQuery(id+"F0.wireOp",EDGE,"E7"),sQuery(id+"F0.wireOp",EDGE,"E8"),sQuery(id+"F0.wireOp",EDGE,"E10"),sQuery(id+"F0.wireOp",EDGE,"E11"),sQuery(id+"F0.wireOp",EDGE,"E13")])]});
            var Q1;
            Q1=makeQuery(id+"F5.opExtrude","SWEPT_BODY",BODY,{"disambiguationData":[OSD([sQuery(id+"F0.wireOp",EDGE,"E0"),sQuery(id+"F0.wireOp",EDGE,"E3"),sQuery(id+"F0.wireOp",EDGE,"E4.bottom"),sQuery(id+"F0.wireOp",EDGE,"E5.bottom"),sQuery(id+"F0.wireOp",EDGE,"E5.right"),sQuery(id+"F0.wireOp",EDGE,"E6.bottom"),sQuery(id+"F0.wireOp",EDGE,"E6.right"),sQuery(id+"F0.wireOp",EDGE,"E7"),sQuery(id+"F0.wireOp",EDGE,"E8"),sQuery(id+"F0.wireOp",EDGE,"E10"),sQuery(id+"F0.wireOp",EDGE,"E11"),sQuery(id+"F0.wireOp",EDGE,"E13")])]});
            var Q2;
            Q2=makeQuery(id+"F2.opExtrude","SWEPT_BODY",BODY,{"disambiguationData":[OSD([sQuery(id+"F0.wireOp",EDGE,"E0"),sQuery(id+"F0.wireOp",EDGE,"E3"),sQuery(id+"F0.wireOp",EDGE,"E4.bottom"),sQuery(id+"F0.wireOp",EDGE,"E5.bottom"),sQuery(id+"F0.wireOp",EDGE,"E5.right"),sQuery(id+"F0.wireOp",EDGE,"E6.bottom"),sQuery(id+"F0.wireOp",EDGE,"E6.right"),sQuery(id+"F0.wireOp",EDGE,"E7"),sQuery(id+"F0.wireOp",EDGE,"E8"),sQuery(id+"F0.wireOp",EDGE,"E10"),sQuery(id+"F0.wireOp",EDGE,"E11"),sQuery(id+"F0.wireOp",EDGE,"E13")])]});
            booleanBodies(context, id + "F14", {"operationType" : BooleanOperationType.UNION, "tools" : qUnion([Q0, Q1, Q2])});
        }
        {
            var Q0;
            {var subQ0=sQuery(id+"F0.wireOp",EDGE,"E5.right");Q0=makeQuery(id+"F13.opBoolean","MERGE",FACE,{"derivedFrom":[makeQuery(id+"F1.opExtrude","SWEPT_FACE",FACE,{"disambiguationData":[OSD([subQ0])]}),makeQuery(id+"F6.opExtrude","SWEPT_FACE",FACE,{"disambiguationData":[OSD([subQ0])]}),makeQuery(id+"F8.opExtrude","SWEPT_FACE",FACE,{"disambiguationData":[OSD([subQ0]),TDD([makeQuery(id+"F6.opExtrude","CAP_EDGE",EDGE,{"disambiguationData":[OSD([subQ0])],"isStart":false})])]})]});}
            var sketch = newSketch(context, id + "F15", { "sketchPlane" : qUnion([Q0])});
            skLineSegment(sketch, "E25", {"start": v(39.37, 0) * mm, "end": v(36.07, 0) * mm});
            skCircle(sketch, "E26", {"center": v(36.07, 0) * mm, "radius": 2.8 * mm});
            skLineSegment(sketch, "E27", {"start": v(39.37, 0) * mm, "end": v(39.37, -25.4) * mm});
            skLineSegment(sketch, "E28", {"start": v(39.37, -25.4) * mm, "end": v(36.07, -25.4) * mm});
            skCircle(sketch, "E29", {"center": v(36.07, -25.4) * mm, "radius": 2.8 * mm});
            skCircle(sketch, "E30", {"center": v(36.07, -25.4) * mm, "radius": 1.27 * mm});
            skCircle(sketch, "E31", {"center": v(36.07, 0) * mm, "radius": 1.27 * mm});
            skSolve(sketch);
        }
        {
            var Q0;
            Q0=makeQuery(id+"F15.imprint","IMPRINT",FACE,{"disambiguationData":[TD([[makeQuery(id+"F15.imprint","IMPRINT",EDGE,{"derivedFrom":sQuery(id+"F15.wireOp",EDGE,"E29")}),1.0]])]});
            var Q1;
            Q1=makeQuery(id+"F15.imprint","IMPRINT",FACE,{"disambiguationData":[TD([[makeQuery(id+"F15.imprint","IMPRINT",EDGE,{"derivedFrom":sQuery(id+"F15.wireOp",EDGE,"E26")}),1.0]])]});
            var Q2;
            Q2=makeQuery(id+"F15.imprint","IMPRINT",FACE,{"disambiguationData":[TD([[makeQuery(id+"F15.imprint","IMPRINT",EDGE,{"derivedFrom":sQuery(id+"F15.wireOp",EDGE,"E30")}),1.0]])]});
            var Q3;
            Q3=makeQuery(id+"F15.imprint","IMPRINT",FACE,{"disambiguationData":[TD([[makeQuery(id+"F15.imprint","IMPRINT",EDGE,{"derivedFrom":sQuery(id+"F15.wireOp",EDGE,"E31")}),1.0]])]});
            extrude(context, id + "F16", {"entities" : qUnion([Q0, Q1, Q2, Q3]), "operationType" : NewBodyOperationType.REMOVE, "oppositeDirection" : true, "depth" : 1.27 * mm, "offsetDistance" : 25.4 * mm});
        }
        {
            var Q0;
            Q0=makeQuery(id+"F15.imprint","IMPRINT",FACE,{"disambiguationData":[TD([[makeQuery(id+"F15.imprint","IMPRINT",EDGE,{"derivedFrom":sQuery(id+"F15.wireOp",EDGE,"E30")}),1.0]])]});
            var Q1;
            Q1=makeQuery(id+"F15.imprint","IMPRINT",FACE,{"disambiguationData":[TD([[makeQuery(id+"F15.imprint","IMPRINT",EDGE,{"derivedFrom":sQuery(id+"F15.wireOp",EDGE,"E31")}),1.0]])]});
            extrude(context, id + "F17", {"entities" : qUnion([Q0, Q1]), "operationType" : NewBodyOperationType.REMOVE, "oppositeDirection" : true, "depth" : 8.9 * mm, "offsetDistance" : 25.4 * mm});
        }
        {
            var Q0;
            {var subQ0=sQuery(id+"F0.wireOp",EDGE,"E6.right");Q0=makeQuery(id+"F13.opBoolean","MERGE",FACE,{"derivedFrom":[makeQuery(id+"F1.opExtrude","SWEPT_FACE",FACE,{"disambiguationData":[OSD([subQ0])]}),makeQuery(id+"F6.opExtrude","SWEPT_FACE",FACE,{"disambiguationData":[OSD([subQ0])]}),makeQuery(id+"F8.opExtrude","SWEPT_FACE",FACE,{"disambiguationData":[OSD([subQ0]),TDD([makeQuery(id+"F6.opExtrude","CAP_EDGE",EDGE,{"disambiguationData":[OSD([subQ0])],"isStart":false})])]})]});}
            var sketch = newSketch(context, id + "F18", { "sketchPlane" : qUnion([Q0])});
            skLineSegment(sketch, "E32", {"start": v(-39.37, 0) * mm, "end": v(-36.07, 0) * mm});
            skCircle(sketch, "E33", {"center": v(-36.07, 0) * mm, "radius": 1.27 * mm});
            skCircle(sketch, "E34", {"center": v(-36.07, 0) * mm, "radius": 2.8 * mm});
            skLineSegment(sketch, "E35", {"start": v(-33.27, 0) * mm, "end": v(-33.27, -25.4) * mm});
            skLineSegment(sketch, "E36", {"start": v(-33.27, -25.4) * mm, "end": v(-36.07, -25.4) * mm});
            skCircle(sketch, "E37", {"center": v(-36.07, -25.4) * mm, "radius": 2.8 * mm});
            skCircle(sketch, "E38", {"center": v(-36.07, -25.4) * mm, "radius": 1.27 * mm});
            skSolve(sketch);
        }
        {
            var Q0;
            Q0=makeQuery(id+"F18.imprint","IMPRINT",FACE,{"disambiguationData":[TD([[makeQuery(id+"F18.imprint","IMPRINT",EDGE,{"derivedFrom":sQuery(id+"F18.wireOp",EDGE,"E37")}),1.0]])]});
            var Q1;
            Q1=makeQuery(id+"F18.imprint","IMPRINT",FACE,{"disambiguationData":[TD([[makeQuery(id+"F18.imprint","IMPRINT",EDGE,{"derivedFrom":sQuery(id+"F18.wireOp",EDGE,"E38")}),1.0]])]});
            var Q2;
            Q2=makeQuery(id+"F18.imprint","IMPRINT",FACE,{"disambiguationData":[TD([[makeQuery(id+"F18.imprint","IMPRINT",EDGE,{"derivedFrom":sQuery(id+"F18.wireOp",EDGE,"E33")}),-1.0]])]});
            var Q3;
            Q3=makeQuery(id+"F18.imprint","IMPRINT",FACE,{"disambiguationData":[TD([[makeQuery(id+"F18.imprint","IMPRINT",EDGE,{"derivedFrom":sQuery(id+"F18.wireOp",EDGE,"E33")}),1.0]])]});
            extrude(context, id + "F19", {"entities" : qUnion([Q0, Q1, Q2, Q3]), "operationType" : NewBodyOperationType.REMOVE, "oppositeDirection" : true, "depth" : 1.27 * mm, "offsetDistance" : 25.4 * mm});
        }
        {
            var Q0;
            Q0=makeQuery(id+"F18.imprint","IMPRINT",FACE,{"disambiguationData":[TD([[makeQuery(id+"F18.imprint","IMPRINT",EDGE,{"derivedFrom":sQuery(id+"F18.wireOp",EDGE,"E38")}),1.0]])]});
            var Q1;
            Q1=makeQuery(id+"F18.imprint","IMPRINT",FACE,{"disambiguationData":[TD([[makeQuery(id+"F18.imprint","IMPRINT",EDGE,{"derivedFrom":sQuery(id+"F18.wireOp",EDGE,"E33")}),1.0]])]});
            extrude(context, id + "F20", {"entities" : qUnion([Q0, Q1]), "operationType" : NewBodyOperationType.REMOVE, "oppositeDirection" : true, "depth" : 8.9 * mm, "offsetDistance" : 25.4 * mm});
        }
        {
            var Q0;
            Q0=qCreatedBy(makeId("Right.planeOp"),FACE);
            var sketch = newSketch(context, id + "F21", { "sketchPlane" : qUnion([Q0])});
            skLineSegment(sketch, "E39", {"start": v(0, 0) * mm, "end": v(0, -12.7) * mm});
            skLineSegment(sketch, "E40", {"start": v(0, -12.7) * mm, "end": v(-59.69, -12.7) * mm});
            skCircle(sketch, "E41", {"center": v(-59.69, -12.7) * mm, "radius": 12.7 * mm});
            skCircle(sketch, "E42", {"center": v(-59.69, -12.7) * mm, "radius": 16.76 * mm});
            skLineSegment(sketch, "E43", {"start": v(-59.69, -12.7) * mm, "end": v(-59.7, 0) * mm});
            skLineSegment(sketch, "E44", {"start": v(-59.7, 0) * mm, "end": v(-59.7, 4.06) * mm});
            skLineSegment(sketch, "E45", {"start": v(-46.99, -12.7) * mm, "end": v(-46.99, -23.64) * mm});
            skSolve(sketch);
        }
        {
            var Q0;
            {var subQ0=sQuery(id+"F21.wireOp",EDGE,"E43");Q0=makeQuery(id+"F21.imprint","IMPRINT",FACE,{"disambiguationData":[TD([[makeQuery(id+"F21.imprint","IMPRINT",EDGE,{"derivedFrom":subQ0}),-1.0]])]});}
            var Q1;
            {var subQ0=sQuery(id+"F21.wireOp",EDGE,"E43");Q1=makeQuery(id+"F21.imprint","IMPRINT",FACE,{"disambiguationData":[TD([[makeQuery(id+"F21.imprint","IMPRINT",EDGE,{"derivedFrom":subQ0}),1.0]])]});}
            extrude(context, id + "F22", {"entities" : qUnion([Q0, Q1]), "operationType" : NewBodyOperationType.REMOVE, "endBound" : BoundingType.SYMMETRIC, "oppositeDirection" : true, "depth" : 127 * mm, "offsetDistance" : 25.4 * mm});
        }
        {
            var Q0;
            {var subQ5=sQuery(id+"F21.wireOp",EDGE,"E44");Q0=makeQuery(id+"F21.imprint","IMPRINT",FACE,{"disambiguationData":[TD([[makeQuery(id+"F21.imprint","IMPRINT",EDGE,{"derivedFrom":subQ5}),1.0]])]});}
            extrude(context, id + "F23", {"entities" : qUnion([Q0]), "operationType" : NewBodyOperationType.ADD, "endBound" : BoundingType.SYMMETRIC, "depth" : 40.64 * mm, "offsetDistance" : 25.4 * mm});
        }
        {
            var Q0;
            {var subQ2=sQuery(id+"F21.wireOp",EDGE,"E41");var subQ11=sQuery(id+"F21.wireOp",EDGE,"E42");Q0=makeQuery(id+"F23.boolean.opBoolean","SPLIT",FACE,{"disambiguationData":[TD([makeQuery(id+"F22.boolean.opBoolean","COPY",FACE,{"derivedFrom":makeQuery(id+"F22.opExtrude","SWEPT_FACE",FACE,{"disambiguationData":[OSD([subQ2])]})})])],"derivedFrom":makeQuery(id+"F23.opExtrude","CAP_FACE",FACE,{"disambiguationData":[OSD([sQuery(id+"F21.wireOp",EDGE,"E40"),subQ2,subQ11,sQuery(id+"F21.wireOp",EDGE,"E44")])],"isStart":false})});}
            var sketch = newSketch(context, id + "F24", { "sketchPlane" : qUnion([Q0])});
            skLineSegment(sketch, "E46", {"start": v(-72.39, -12.7) * mm, "end": v(-59.69, -12.7) * mm});
            skPoint(sketch, "E46.startSnap0", {"position": v(-72.39, -12.7) * mm});
            skLineSegment(sketch, "E47", {"start": v(-59.69, -12.7) * mm, "end": v(-46.99, -12.7) * mm});
            skLineSegment(sketch, "E48", {"start": v(-46.99, -12.7) * mm, "end": v(-42.93, -12.7) * mm});
            skLineSegment(sketch, "E49", {"start": v(-42.93, -12.7) * mm, "end": v(-42.93, -29.46) * mm});
            skLineSegment(sketch, "E50", {"start": v(-42.93, -29.46) * mm, "end": v(-59.69, -29.46) * mm});
            skLineSegment(sketch, "E51", {"start": v(-59.69, -29.46) * mm, "end": v(-59.7, 4.06) * mm});
            skLineSegment(sketch, "E52", {"start": v(-59.7, 4.06) * mm, "end": v(-47, 4.06) * mm});
            skLineSegment(sketch, "E53", {"start": v(-42.93, -12.7) * mm, "end": v(-42.93, 4.06) * mm});
            skLineSegment(sketch, "E54", {"start": v(-42.93, 4.06) * mm, "end": v(-47, 4.06) * mm});
            skSolve(sketch);
        }
        {
            var Q0;
            {var subQ0=sQuery(id+"F24.wireOp",EDGE,"E47");Q0=makeQuery(id+"F24.imprint","IMPRINT",FACE,{"disambiguationData":[TD([[makeQuery(id+"F24.imprint","IMPRINT",EDGE,{"derivedFrom":subQ0}),-1.0]])]});}
            var Q1;
            {var subQ4=sQuery(id+"F24.wireOp",EDGE,"E47");Q1=makeQuery(id+"F24.imprint","IMPRINT",FACE,{"disambiguationData":[TD([[makeQuery(id+"F24.imprint","IMPRINT",EDGE,{"derivedFrom":subQ4}),1.0]])]});}
            var Q2;
            {var subQ0=sQuery(id+"F0.wireOp",EDGE,"E6.right");Q2=makeQuery(id+"F14.opBoolean","MERGE",FACE,{"derivedFrom":[makeQuery(id+"F2.opExtrude","SWEPT_FACE",FACE,{"disambiguationData":[OSD([subQ0])]}),makeQuery(id+"F5.opExtrude","SWEPT_FACE",FACE,{"disambiguationData":[OSD([subQ0])]}),makeQuery(id+"F8.opExtrude","SWEPT_FACE",FACE,{"disambiguationData":[OSD([subQ0]),TDD([makeQuery(id+"F5.opExtrude","CAP_EDGE",EDGE,{"disambiguationData":[OSD([subQ0])],"isStart":false})])]})]});}
            extrude(context, id + "F25", {"entities" : qUnion([Q0, Q1]), "operationType" : NewBodyOperationType.REMOVE, "endBound" : BoundingType.UP_TO_SURFACE, "depth" : 25.4 * mm, "endBoundEntityFace" : qUnion([Q2]), "offsetDistance" : 25.4 * mm});
        }
        {
            var Q0;
            Q0=makeQuery(id+"F23.opExtrude","CAP_FACE",FACE,{"disambiguationData":[OSD([sQuery(id+"F21.wireOp",EDGE,"E40"),sQuery(id+"F21.wireOp",EDGE,"E41"),sQuery(id+"F21.wireOp",EDGE,"E42"),sQuery(id+"F21.wireOp",EDGE,"E44")])],"isStart":true});
            var sketch = newSketch(context, id + "F26", { "sketchPlane" : qUnion([Q0])});
            skLineSegment(sketch, "E55", {"start": v(72.39, -12.7) * mm, "end": v(59.69, -12.7) * mm});
            skPoint(sketch, "E55.startSnap0", {"position": v(72.39, -12.7) * mm});
            skLineSegment(sketch, "E56", {"start": v(59.69, -12.7) * mm, "end": v(46.99, -12.7) * mm});
            skLineSegment(sketch, "E57", {"start": v(46.99, -12.7) * mm, "end": v(42.93, -12.7) * mm});
            skLineSegment(sketch, "E58", {"start": v(59.69, -12.7) * mm, "end": v(59.7, 4.06) * mm});
            skLineSegment(sketch, "E59", {"start": v(59.7, 4.06) * mm, "end": v(59.7, -29.46) * mm});
            skLineSegment(sketch, "E60", {"start": v(59.7, -29.46) * mm, "end": v(42.93, -29.46) * mm});
            skLineSegment(sketch, "E61", {"start": v(42.93, -29.46) * mm, "end": v(42.93, -12.7) * mm});
            skLineSegment(sketch, "E62", {"start": v(42.93, 4.06) * mm, "end": v(59.7, 4.06) * mm});
            skLineSegment(sketch, "E63", {"start": v(42.93, -12.7) * mm, "end": v(42.93, 4.06) * mm});
            skSolve(sketch);
        }
        {
            var Q0;
            {var subQ3=sQuery(id+"F26.wireOp",EDGE,"E56");Q0=makeQuery(id+"F26.imprint","IMPRINT",FACE,{"disambiguationData":[TD([[makeQuery(id+"F26.imprint","IMPRINT",EDGE,{"derivedFrom":subQ3}),1.0]])]});}
            var Q1;
            Q1=makeQuery(id+"F26.imprint","IMPRINT",FACE,{"disambiguationData":[TD([[makeQuery(id+"F26.imprint","IMPRINT",EDGE,{"derivedFrom":sQuery(id+"F26.wireOp",EDGE,"E56")}),-1.0]])]});
            var Q2;
            {var subQ0=sQuery(id+"F0.wireOp",EDGE,"E5.right");Q2=makeQuery(id+"F14.opBoolean","MERGE",FACE,{"derivedFrom":[makeQuery(id+"F2.opExtrude","SWEPT_FACE",FACE,{"disambiguationData":[OSD([subQ0])]}),makeQuery(id+"F5.opExtrude","SWEPT_FACE",FACE,{"disambiguationData":[OSD([subQ0])]}),makeQuery(id+"F8.opExtrude","SWEPT_FACE",FACE,{"disambiguationData":[OSD([subQ0]),TDD([makeQuery(id+"F5.opExtrude","CAP_EDGE",EDGE,{"disambiguationData":[OSD([subQ0])],"isStart":false})])]})]});}
            extrude(context, id + "F27", {"entities" : qUnion([Q0, Q1]), "operationType" : NewBodyOperationType.REMOVE, "endBound" : BoundingType.UP_TO_SURFACE, "depth" : 25.4 * mm, "endBoundEntityFace" : qUnion([Q2]), "offsetDistance" : 25.4 * mm});
        }
        {
            var Q0;
            Q0=makeQuery(id+"F25.boolean.opBoolean","COPY",EDGE,{"derivedFrom":makeQuery(id+"F25.opExtrude","SWEPT_EDGE",EDGE,{"disambiguationData":[OSD([sQuery(id+"F24.wireOp",EDGE,"E53"),sQuery(id+"F24.wireOp",EDGE,"E54")])]})});
            var Q1;
            Q1=makeQuery(id+"F27.boolean.opBoolean","COPY",EDGE,{"derivedFrom":makeQuery(id+"F27.opExtrude","SWEPT_EDGE",EDGE,{"disambiguationData":[OSD([sQuery(id+"F26.wireOp",EDGE,"E62"),sQuery(id+"F26.wireOp",EDGE,"E63")])]})});
            var Q2;
            Q2=makeQuery(id+"F25.boolean.opBoolean","COPY",EDGE,{"derivedFrom":makeQuery(id+"F25.opExtrude","SWEPT_EDGE",EDGE,{"disambiguationData":[OSD([sQuery(id+"F24.wireOp",EDGE,"E49"),sQuery(id+"F24.wireOp",EDGE,"E50")])]})});
            var Q3;
            Q3=makeQuery(id+"F27.boolean.opBoolean","COPY",EDGE,{"derivedFrom":makeQuery(id+"F27.opExtrude","SWEPT_EDGE",EDGE,{"disambiguationData":[OSD([sQuery(id+"F26.wireOp",EDGE,"E60"),sQuery(id+"F26.wireOp",EDGE,"E61")])]})});
            var Q4;
            Q4=makeQuery(id+"F27.boolean.opBoolean","COPY",EDGE,{"derivedFrom":makeQuery(id+"F27.opExtrude","CAP_EDGE",EDGE,{"disambiguationData":[OSD([sQuery(id+"F26.wireOp",EDGE,"E61"),sQuery(id+"F26.wireOp",EDGE,"E63")])],"isStart":false})});
            var Q5;
            Q5=makeQuery(id+"F25.boolean.opBoolean","COPY",EDGE,{"derivedFrom":makeQuery(id+"F25.opExtrude","CAP_EDGE",EDGE,{"disambiguationData":[OSD([sQuery(id+"F24.wireOp",EDGE,"E53")])],"isStart":false})});
            var Q6;
            Q6=makeQuery(id+"F12.boolean.opBoolean","COPY",EDGE,{"derivedFrom":makeQuery(id+"F12.opExtrude","SWEPT_EDGE",EDGE,{"disambiguationData":[OSD([sQuery(id+"F0.wireOp",EDGE,"E6.right"),sQuery(id+"F11.wireOp",EDGE,"E24.bottom"),sQuery(id+"F11.wireOp",EDGE,"E24.left")])]})});
            var Q7;
            Q7=makeQuery(id+"F12.boolean.opBoolean","COPY",EDGE,{"derivedFrom":makeQuery(id+"F12.opExtrude","SWEPT_EDGE",EDGE,{"disambiguationData":[OSD([sQuery(id+"F0.wireOp",EDGE,"E5.right"),sQuery(id+"F10.wireOp",EDGE,"E22.bottom"),sQuery(id+"F10.wireOp",EDGE,"E22.left")])]})});
            var Q8;
            {var subQ0=sQuery(id+"F21.wireOp",EDGE,"E41");Q8=makeQuery(id+"F23.boolean.opBoolean","MERGE",FACE,{"derivedFrom":[makeQuery(id+"F22.boolean.opBoolean","COPY",FACE,{"derivedFrom":makeQuery(id+"F22.opExtrude","SWEPT_FACE",FACE,{"disambiguationData":[OSD([subQ0])]})}),makeQuery(id+"F23.opExtrude","SWEPT_FACE",FACE,{"disambiguationData":[OSD([subQ0])]})]});}
            var Q9;
            Q9=makeQuery(id+"F23.opExtrude","CAP_EDGE",EDGE,{"disambiguationData":[OSD([sQuery(id+"F21.wireOp",EDGE,"E42")])],"isStart":true});
            var Q10;
            Q10=makeQuery(id+"F23.opExtrude","CAP_EDGE",EDGE,{"disambiguationData":[OSD([sQuery(id+"F21.wireOp",EDGE,"E42")])],"isStart":false});
            fillet(context, id + "F28", {"entities" : qUnion([Q0, Q1, Q2, Q3, Q4, Q5, Q6, Q7, Q8, Q9, Q10]), "radius" : 2.54 * mm, "tangentPropagation" : true, "allowEdgeOverflow" : false});
        }
        {
            var Q0;
            Q0=makeQuery(id+"F20.boolean.opBoolean","COPY",FACE,{"derivedFrom":makeQuery(id+"F20.opExtrude","CAP_FACE",FACE,{"disambiguationData":[OSD([sQuery(id+"F18.wireOp",EDGE,"E33")])],"isStart":false})});
            extrude(context, id + "F29", {"entities" : qUnion([Q0]), "operationType" : NewBodyOperationType.REMOVE, "oppositeDirection" : true, "depth" : 6.35 * mm, "offsetDistance" : 25.4 * mm});
        }
        {
            var Q0;
            Q0=makeQuery(id+"F17.boolean.opBoolean","COPY",FACE,{"derivedFrom":makeQuery(id+"F17.opExtrude","CAP_FACE",FACE,{"disambiguationData":[OSD([sQuery(id+"F15.wireOp",EDGE,"E31")])],"isStart":false})});
            extrude(context, id + "F30", {"entities" : qUnion([Q0]), "operationType" : NewBodyOperationType.REMOVE, "oppositeDirection" : true, "depth" : 6.35 * mm, "offsetDistance" : 25.4 * mm});
        }
    });
